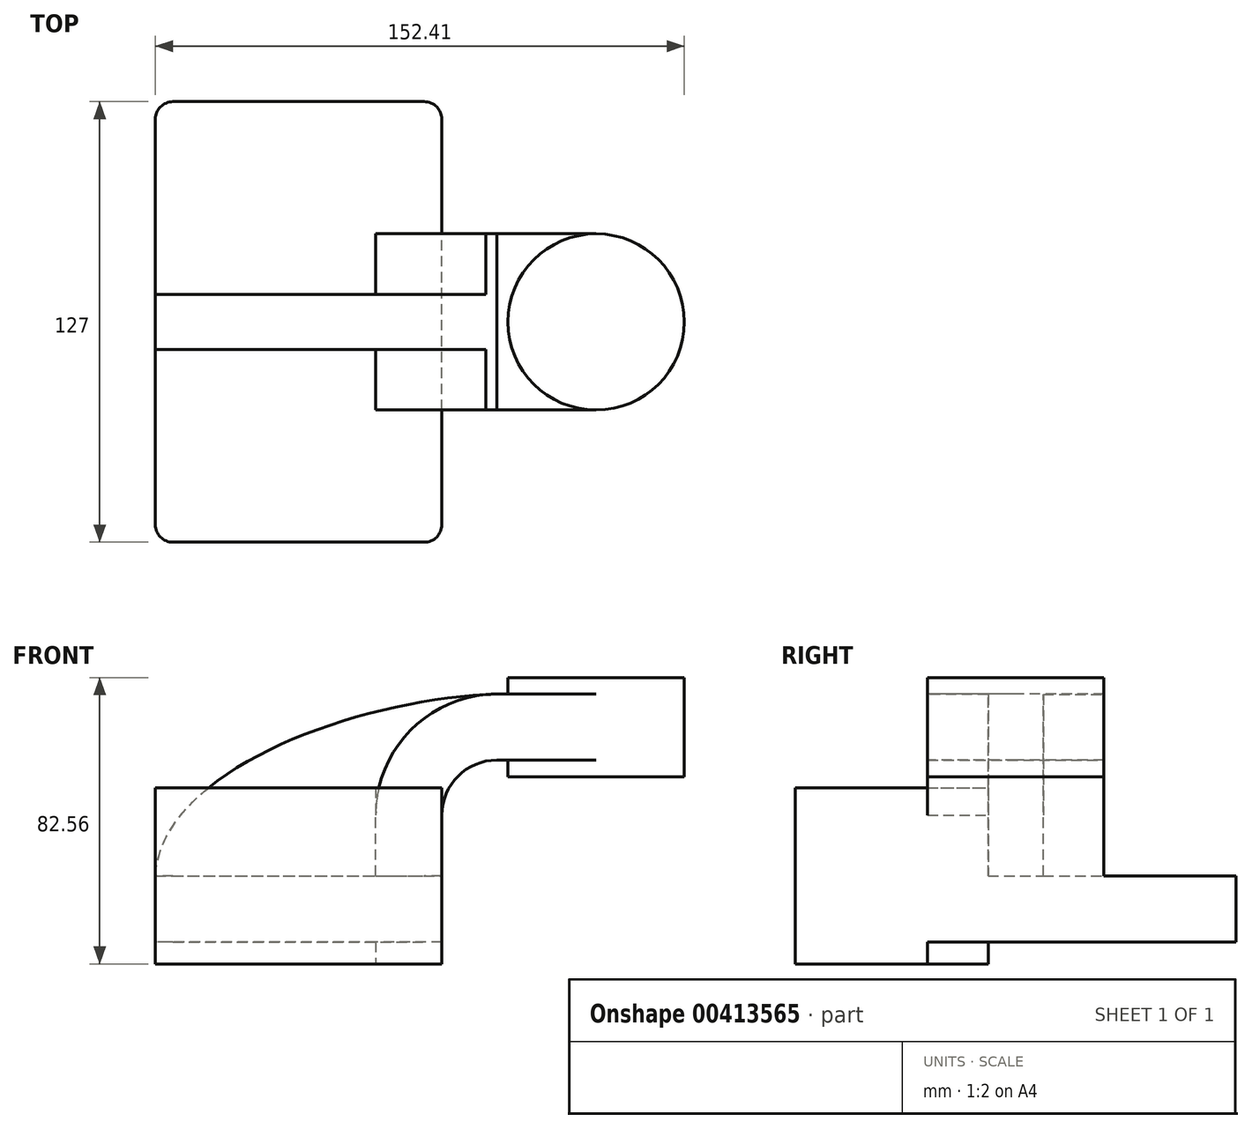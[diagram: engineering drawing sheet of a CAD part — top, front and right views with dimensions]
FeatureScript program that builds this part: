
annotation { "Feature Type Name" : "Feature", "Feature Type Description" : "" }
export const myFeature = defineFeature(function(context is Context, id is Id, definition is map)
    precondition{}
    {
        {
            var Q0;
            Q0=qCreatedBy(makeId("Front.planeOp"),FACE);
            var sketch = newSketch(context, id + "F0", { "sketchPlane" : qUnion([Q0])});
            skLineSegment(sketch, "E0.rect.bottom", {"start": v(-41.28, 9.52) * mm, "end": v(41.28, 9.52) * mm});
            skLineSegment(sketch, "E0.rect.top", {"start": v(-41.28, -9.52) * mm, "end": v(41.28, -9.52) * mm});
            skLineSegment(sketch, "E0.rect.left", {"start": v(-41.28, 9.52) * mm, "end": v(-41.28, -9.52) * mm});
            skLineSegment(sketch, "E0.rect.right", {"start": v(41.28, 9.52) * mm, "end": v(41.28, -9.52) * mm});
            skPoint(sketch, "E0.rect.middle", {"position": v(0, 0) * mm});
            skLineSegment(sketch, "E1", {"start": v(41.28, 9.52) * mm, "end": v(41.28, 27) * mm});
            skArc(sketch, "E2", {"start": v(41.28, 27) * mm, "mid": v(45.92, 38.23) * mm, "end": v(57.15, 42.88) * mm});
            skLineSegment(sketch, "E3", {"start": v(57.15, 42.88) * mm, "end": v(85.72, 42.88) * mm});
            skLineSegment(sketch, "E4.rect.bottom", {"start": v(60.32, 38.1) * mm, "end": v(111.12, 38.1) * mm});
            skLineSegment(sketch, "E4.rect.top", {"start": v(60.32, 66.68) * mm, "end": v(111.12, 66.68) * mm});
            skLineSegment(sketch, "E4.rect.left", {"start": v(60.32, 38.1) * mm, "end": v(60.32, 66.68) * mm});
            skLineSegment(sketch, "E4.rect.right", {"start": v(111.13, 38.1) * mm, "end": v(111.12, 66.68) * mm});
            skPoint(sketch, "E4.rect.middle", {"position": v(85.72, 52.39) * mm});
            skLineSegment(sketch, "E5.0", {"start": v(57.15, 61.93) * mm, "end": v(85.72, 61.93) * mm});
            skArc(sketch, "E5.1", {"start": v(22.23, 27) * mm, "mid": v(32.45, 51.7) * mm, "end": v(57.15, 61.93) * mm});
            skLineSegment(sketch, "E5.2", {"start": v(22.23, 9.52) * mm, "end": v(22.23, 27) * mm});
            skLineSegment(sketch, "E6", {"start": v(85.72, 38.1) * mm, "end": v(85.72, 66.68) * mm});
            skFitSpline(sketch, "E7", {"points": [v(-41.28, 9.53) * mm, v(57.15, 61.93) * mm], "startDerivative": vector(5.2, 92.34) * mm, "endDerivative": vector(120.92, 4.22) * mm});
            skSolve(sketch);
        }
        {
            var Q0;
            Q0=makeQuery(id+"F0.imprint","IMPRINT",FACE,{"disambiguationData":[TD([[makeQuery(id+"F0.imprint","IMPRINT",EDGE,{"derivedFrom":sQuery(id+"F0.wireOp",EDGE,"E0.rect.top")}),1.0]])]});
            extrude(context, id + "F1", {"entities" : qUnion([Q0]), "endBound" : BoundingType.SYMMETRIC, "depth" : 127 * mm});
        }
        {
            var Q0;
            {var subQ9=sQuery(id+"F0.wireOp",EDGE,"E1");Q0=makeQuery(id+"F0.imprint","IMPRINT",FACE,{"disambiguationData":[TD([[makeQuery(id+"F0.imprint","IMPRINT",EDGE,{"derivedFrom":subQ9}),1.0]])]});}
            var Q1;
            {var subQ0=sQuery(id+"F0.wireOp",EDGE,"E6");var subQ1=sQuery(id+"F0.wireOp",EDGE,"E3");var subQ2=makeQuery(id+"F0.imprint","INTERSECT",VERTEX,{"derivedFrom":[subQ1,subQ0]});Q1=makeQuery(id+"F0.imprint","IMPRINT",FACE,{"disambiguationData":[TD([[makeQuery(id+"F0.imprint","IMPRINT",EDGE,{"disambiguationData":[TD([[subQ2,1.0]])],"derivedFrom":subQ1}),1.0]])]});}
            extrude(context, id + "F2", {"entities" : qUnion([Q0, Q1]), "operationType" : NewBodyOperationType.ADD, "endBound" : BoundingType.SYMMETRIC, "depth" : 50.8 * mm});
        }
        {
            var Q0;
            {var subQ3=sQuery(id+"F0.wireOp",EDGE,"E5.2");Q0=makeQuery(id+"F0.imprint","IMPRINT",FACE,{"disambiguationData":[TD([[makeQuery(id+"F0.imprint","IMPRINT",EDGE,{"derivedFrom":subQ3}),1.0]])]});}
            extrude(context, id + "F3", {"entities" : qUnion([Q0]), "operationType" : NewBodyOperationType.ADD, "endBound" : BoundingType.SYMMETRIC, "depth" : 15.88 * mm});
        }
        {
            var Q0;
            {var subQ5=sQuery(id+"F0.wireOp",EDGE,"E4.rect.right");Q0=makeQuery(id+"F0.imprint","IMPRINT",FACE,{"disambiguationData":[TD([[makeQuery(id+"F0.imprint","IMPRINT",EDGE,{"derivedFrom":subQ5}),1.0]])]});}
            var Q1;
            Q1=sQuery(id+"F0.wireOp",EDGE,"E6");
            revolve(context, id + "F4", {"operationType" : NewBodyOperationType.ADD, "entities" : qUnion([Q0]), "axis" : qUnion([Q1]), "revolveType" : RevolveType.FULL});
        }
        {
            var Q0;
            Q0=makeQuery(id+"F1.opExtrude","CAP_EDGE",EDGE,{"disambiguationData":[OSD([sQuery(id+"F0.wireOp",EDGE,"E0.rect.right")])],"isStart":false});
            var Q1;
            Q1=makeQuery(id+"F1.opExtrude","CAP_EDGE",EDGE,{"disambiguationData":[OSD([sQuery(id+"F0.wireOp",EDGE,"E0.rect.left")])],"isStart":false});
            var Q2;
            Q2=makeQuery(id+"F1.opExtrude","CAP_EDGE",EDGE,{"disambiguationData":[OSD([sQuery(id+"F0.wireOp",EDGE,"E0.rect.right")])],"isStart":true});
            var Q3;
            Q3=makeQuery(id+"F1.opExtrude","CAP_EDGE",EDGE,{"disambiguationData":[OSD([sQuery(id+"F0.wireOp",EDGE,"E0.rect.left")])],"isStart":true});
            fillet(context, id + "F5", {"entities" : qUnion([Q0, Q1, Q2, Q3]), "radius" : 5.08 * mm, "tangentPropagation" : true, "allowEdgeOverflow" : false});
        }
        {
            var Q0;
            {var subQ4=sQuery(id+"F0.wireOp",EDGE,"E0.rect.bottom");var subQ5=sQuery(id+"F0.wireOp",EDGE,"E0.rect.right");var subQ6=sQuery(id+"F0.wireOp",EDGE,"E0.rect.left");Q0=makeQuery(id+"F3.boolean.opBoolean","SPLIT",FACE,{"disambiguationData":[TD([makeQuery(id+"F1.opExtrude","CAP_FACE",FACE,{"disambiguationData":[OSD([subQ4,sQuery(id+"F0.wireOp",EDGE,"E0.rect.top"),subQ6,subQ5])],"isStart":false})])],"derivedFrom":makeQuery(id+"F1.opExtrude","SWEPT_FACE",FACE,{"disambiguationData":[OSD([subQ4])]})});}
            extrude(context, id + "F6", {"entities" : qUnion([Q0]), "operationType" : NewBodyOperationType.ADD, "endBound" : BoundingType.SYMMETRIC, "depth" : 50.8 * mm});
        }
    });
